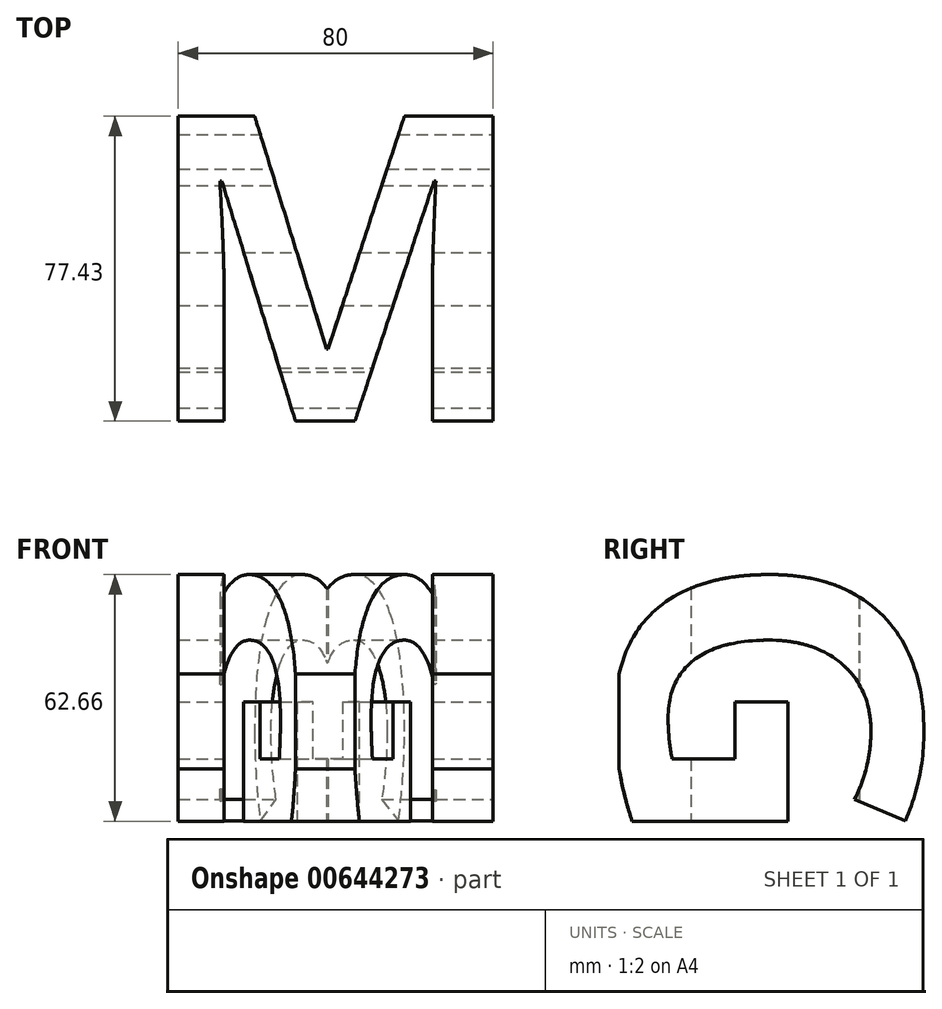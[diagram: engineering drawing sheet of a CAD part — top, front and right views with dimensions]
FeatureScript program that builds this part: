
annotation { "Feature Type Name" : "Feature", "Feature Type Description" : "" }
export const myFeature = defineFeature(function(context is Context, id is Id, definition is map)
    precondition{}
    {
        {
            var Q0;
            Q0=qCreatedBy(makeId("Top.planeOp"),FACE);
            var sketch = newSketch(context, id + "F0", { "sketchPlane" : qUnion([Q0])});
            skText(sketch, "E0", { "text": "M", "fontName": "OpenSans-Bold.ttf"});
            const initialGuessF0  = {"E0": [0, 0, 1, 0, 0.07845]};
            skSetInitialGuess(sketch, initialGuessF0);
            skSolve(sketch);
        }
        {
            var Q0;
            Q0 = qSketchRegion(id + "F0", true);
            extrude(context, id + "F1", {"entities" : qUnion([Q0]), "depth" : 100 * mm, "offsetDistance" : 25 * mm});
        }
        {
            var Q0;
            Q0=makeQuery(id+"F1.opExtrude","SWEPT_FACE",FACE,{"disambiguationData":[OSD([sQuery(id+"F0.wireOp",EDGE,"E0.sketch_text.stroke-11")])]});
            var sketch = newSketch(context, id + "F2", { "sketchPlane" : qUnion([Q0])});
            skText(sketch, "E1", { "text": "G", "fontName": "OpenSans-Bold.ttf"});
            const initialGuessF2  = {"E1": [0, 0.09625, 0, -1, 0.077]};
            skSetInitialGuess(sketch, initialGuessF2);
            skSolve(sketch);
        }
        {
            var Q0;
            Q0 = qSketchRegion(id + "F2", true);
            var Q1;
            Q1=makeQuery(id+"F1.opExtrude","SWEPT_FACE",FACE,{"disambiguationData":[OSD([sQuery(id+"F0.wireOp",EDGE,"E0.sketch_text.stroke-5")])]});
            extrude(context, id + "F3", {"entities" : qUnion([Q0, Q1]), "operationType" : NewBodyOperationType.INTERSECT, "oppositeDirection" : true, "depth" : 80 * mm, "offsetDistance" : 25 * mm});
        }
    });
